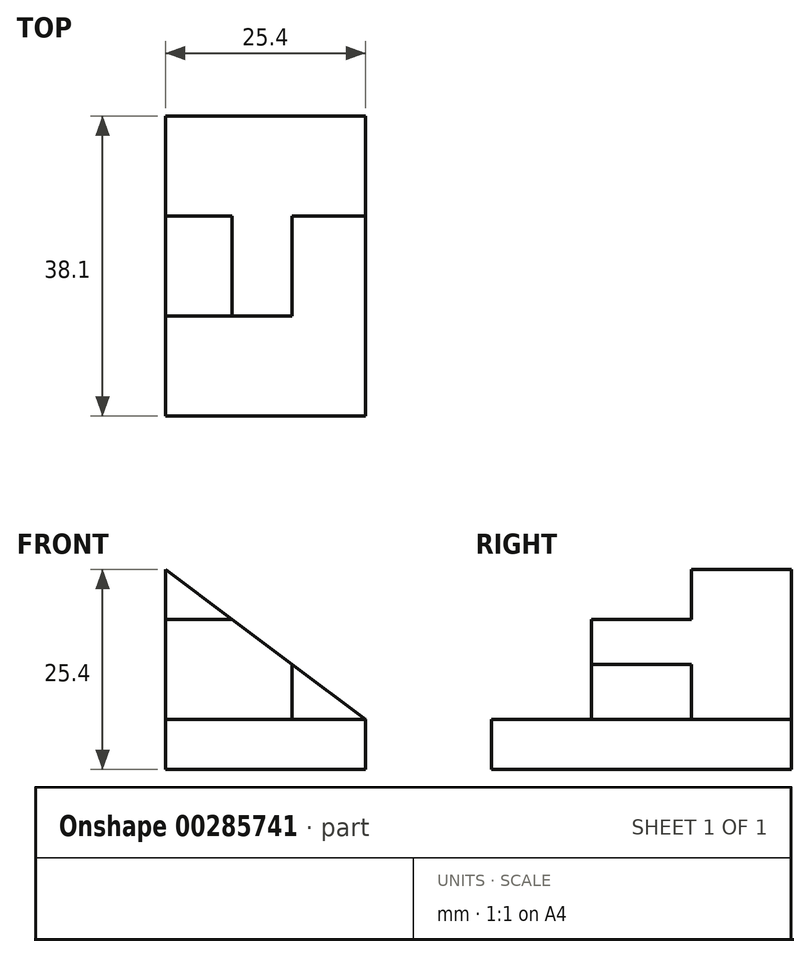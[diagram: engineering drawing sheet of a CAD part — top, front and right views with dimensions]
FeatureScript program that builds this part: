
annotation { "Feature Type Name" : "Feature", "Feature Type Description" : "" }
export const myFeature = defineFeature(function(context is Context, id is Id, definition is map)
    precondition{}
    {
        {
            var Q0;
            Q0=qCreatedBy(makeId("Front.planeOp"),FACE);
            var sketch = newSketch(context, id + "F0", { "sketchPlane" : qUnion([Q0])});
            skLineSegment(sketch, "E0", {"start": v(0, 0) * mm, "end": v(0, 6.35) * mm});
            skLineSegment(sketch, "E1", {"start": v(0, 6.35) * mm, "end": v(25.4, 6.35) * mm});
            skLineSegment(sketch, "E2", {"start": v(25.4, 6.35) * mm, "end": v(25.4, 0) * mm});
            skLineSegment(sketch, "E3", {"start": v(25.4, 0) * mm, "end": v(0, 0) * mm});
            skSolve(sketch);
        }
        {
            var Q0;
            Q0 = qSketchRegion(id + "F0", true);
            extrude(context, id + "F1", {"entities" : qUnion([Q0]), "oppositeDirection" : true, "depth" : 38.1 * mm});
        }
        {
            var Q0;
            Q0=makeQuery(id+"F1.opExtrude","CAP_FACE",FACE,{"disambiguationData":[OSD([sQuery(id+"F0.wireOp",EDGE,"E0"),sQuery(id+"F0.wireOp",EDGE,"E1"),sQuery(id+"F0.wireOp",EDGE,"E2"),sQuery(id+"F0.wireOp",EDGE,"E3")])],"isStart":false});
            var sketch = newSketch(context, id + "F2", { "sketchPlane" : qUnion([Q0])});
            skLineSegment(sketch, "E4", {"start": v(0, 6.35) * mm, "end": v(0, 25.4) * mm});
            skLineSegment(sketch, "E5", {"start": v(0, 25.4) * mm, "end": v(-25.4, 6.35) * mm});
            skLineSegment(sketch, "E6", {"start": v(-25.4, 6.35) * mm, "end": v(0, 6.35) * mm});
            skSolve(sketch);
        }
        {
            var Q0;
            Q0 = qSketchRegion(id + "F2", true);
            extrude(context, id + "F3", {"entities" : qUnion([Q0]), "operationType" : NewBodyOperationType.ADD, "oppositeDirection" : true, "depth" : 12.7 * mm});
        }
        {
            var Q0;
            Q0=makeQuery(id+"F3.opExtrude","CAP_FACE",FACE,{"disambiguationData":[OSD([sQuery(id+"F2.wireOp",EDGE,"E4"),sQuery(id+"F2.wireOp",EDGE,"E5"),sQuery(id+"F2.wireOp",EDGE,"E6")])],"isStart":false});
            var sketch = newSketch(context, id + "F4", { "sketchPlane" : qUnion([Q0])});
            skLineSegment(sketch, "E7", {"start": v(0, 6.35) * mm, "end": v(0, 19.05) * mm});
            skLineSegment(sketch, "E8", {"start": v(0, 19.05) * mm, "end": v(8.47, 19.05) * mm});
            skLineSegment(sketch, "E9", {"start": v(0, 6.35) * mm, "end": v(16.06, 6.35) * mm});
            skLineSegment(sketch, "E10", {"start": v(16.06, 6.35) * mm, "end": v(16.06, 13.35) * mm});
            skLineSegment(sketch, "E11", {"start": v(16.06, 13.35) * mm, "end": v(8.47, 19.05) * mm});
            skSolve(sketch);
        }
        {
            var Q0;
            Q0 = qSketchRegion(id + "F4", true);
            extrude(context, id + "F5", {"entities" : qUnion([Q0]), "operationType" : NewBodyOperationType.ADD, "depth" : 12.7 * mm});
        }
    });
